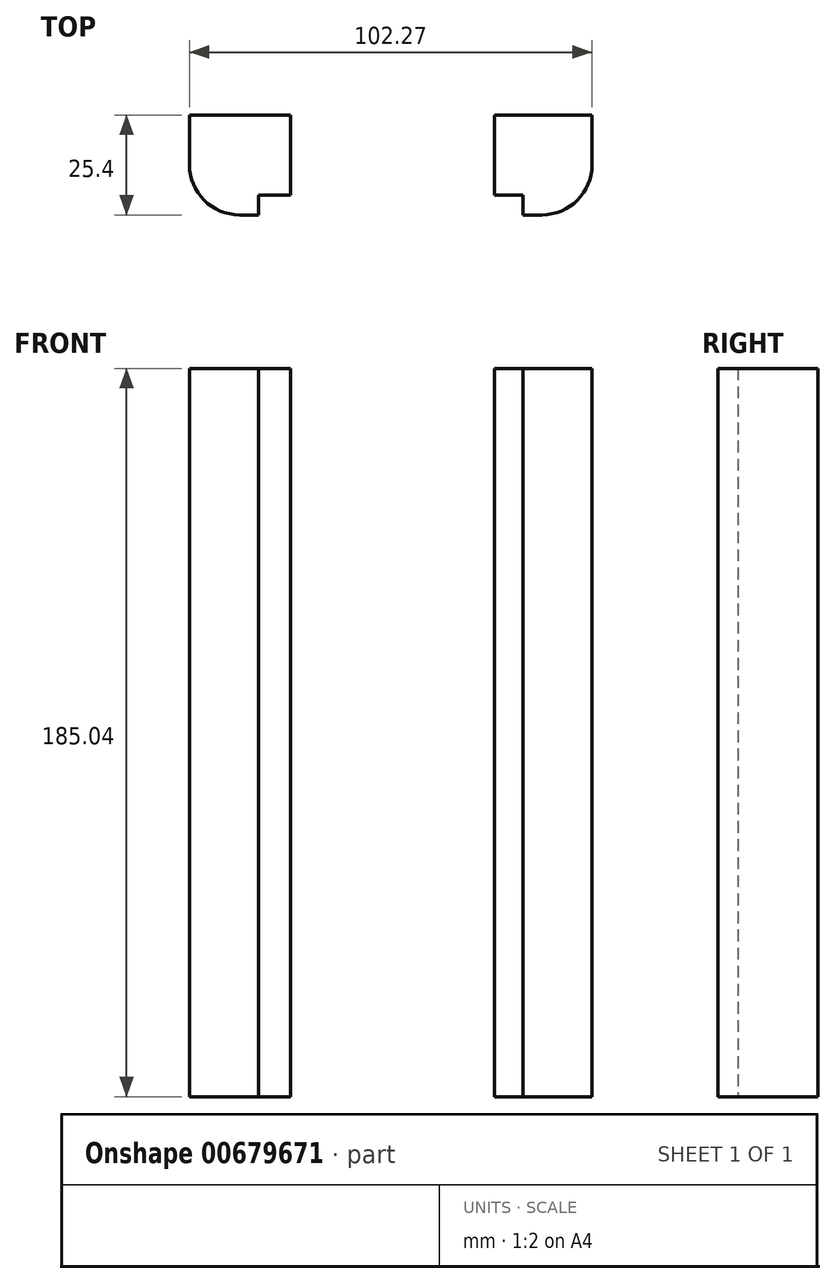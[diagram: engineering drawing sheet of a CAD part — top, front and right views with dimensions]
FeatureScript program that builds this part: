
annotation { "Feature Type Name" : "Feature", "Feature Type Description" : "" }
export const myFeature = defineFeature(function(context is Context, id is Id, definition is map)
    precondition{}
    {
        {
            var Q0;
            Q0=qCreatedBy(makeId("Front.planeOp"),FACE);
            var sketch = newSketch(context, id + "F0", { "sketchPlane" : qUnion([Q0])});
            skLineSegment(sketch, "E0.bottom", {"start": v(-47.2, 111.08) * mm, "end": v(55.07, 111.08) * mm});
            skLineSegment(sketch, "E0.top", {"start": v(-47.2, -73.96) * mm, "end": v(55.07, -73.96) * mm});
            skLineSegment(sketch, "E0.left", {"start": v(-47.2, 111.08) * mm, "end": v(-47.2, -73.96) * mm});
            skLineSegment(sketch, "E0.right", {"start": v(55.07, 111.08) * mm, "end": v(55.07, -73.96) * mm});
            skSolve(sketch);
        }
        {
            var Q0;
            Q0 = qSketchRegion(id + "F0", true);
            extrude(context, id + "F1", {"entities" : qUnion([Q0]), "depth" : 25.4 * mm, "offsetDistance" : 25.4 * mm});
        }
        {
            var Q0;
            Q0=makeQuery(id+"F1.opExtrude","CAP_EDGE",EDGE,{"disambiguationData":[OSD([sQuery(id+"F0.wireOp",EDGE,"E0.right")])],"isStart":false});
            var Q1;
            Q1=makeQuery(id+"F1.opExtrude","CAP_EDGE",EDGE,{"disambiguationData":[OSD([sQuery(id+"F0.wireOp",EDGE,"E0.left")])],"isStart":false});
            fillet(context, id + "F2", {"entities" : qUnion([Q0, Q1]), "radius" : 12.7 * mm, "tangentPropagation" : true, "allowEdgeOverflow" : false});
        }
        {
            var Q0;
            Q0=makeQuery(id+"F1.opExtrude","CAP_FACE",FACE,{"disambiguationData":[OSD([sQuery(id+"F0.wireOp",EDGE,"E0.bottom"),sQuery(id+"F0.wireOp",EDGE,"E0.top"),sQuery(id+"F0.wireOp",EDGE,"E0.left"),sQuery(id+"F0.wireOp",EDGE,"E0.right")])],"isStart":true});
            var sketch = newSketch(context, id + "F3", { "sketchPlane" : qUnion([Q0])});
            skLineSegment(sketch, "E1.bottom", {"start": v(-30.33, 111.08) * mm, "end": v(21.55, 111.08) * mm});
            skLineSegment(sketch, "E1.top", {"start": v(-30.33, -73.96) * mm, "end": v(21.55, -73.96) * mm});
            skLineSegment(sketch, "E1.left", {"start": v(-30.33, 111.08) * mm, "end": v(-30.33, -73.96) * mm});
            skLineSegment(sketch, "E1.right", {"start": v(21.55, 111.08) * mm, "end": v(21.55, -73.96) * mm});
            skSolve(sketch);
        }
        {
            var Q0;
            Q0 = qSketchRegion(id + "F3", true);
            extrude(context, id + "F4", {"entities" : qUnion([Q0]), "operationType" : NewBodyOperationType.REMOVE, "oppositeDirection" : true, "depth" : 21.59 * mm, "offsetDistance" : 25.4 * mm});
        }
        {
            var Q0;
            Q0=makeQuery(id+"F1.opExtrude","CAP_FACE",FACE,{"disambiguationData":[OSD([sQuery(id+"F0.wireOp",EDGE,"E0.bottom"),sQuery(id+"F0.wireOp",EDGE,"E0.top"),sQuery(id+"F0.wireOp",EDGE,"E0.left"),sQuery(id+"F0.wireOp",EDGE,"E0.right")])],"isStart":false});
            var sketch = newSketch(context, id + "F5", { "sketchPlane" : qUnion([Q0])});
            skLineSegment(sketch, "E2.bottom", {"start": v(-29.65, 111.08) * mm, "end": v(37.52, 111.08) * mm});
            skLineSegment(sketch, "E2.top", {"start": v(-29.65, -73.96) * mm, "end": v(37.52, -73.96) * mm});
            skLineSegment(sketch, "E2.left", {"start": v(-29.65, 111.08) * mm, "end": v(-29.65, -73.96) * mm});
            skLineSegment(sketch, "E2.right", {"start": v(37.52, 111.08) * mm, "end": v(37.52, -73.96) * mm});
            skSolve(sketch);
        }
        {
            var Q0;
            Q0=makeQuery(id+"F5.imprint","IMPRINT",FACE,{"disambiguationData":[TD([[makeQuery(id+"F5.imprint","IMPRINT",EDGE,{"derivedFrom":sQuery(id+"F5.wireOp",EDGE,"E2.bottom")}),-1.0]])]});
            extrude(context, id + "F6", {"entities" : qUnion([Q0]), "operationType" : NewBodyOperationType.REMOVE, "oppositeDirection" : true, "depth" : 5.08 * mm, "offsetDistance" : 25.4 * mm});
        }
    });
